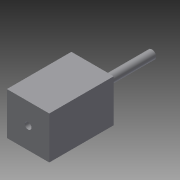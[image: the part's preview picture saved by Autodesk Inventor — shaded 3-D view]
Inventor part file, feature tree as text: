
AUTODESK INVENTOR PART (.ipt)
format: ipt  version: 2013 (Build 170138000, 138)  size: 86,528 bytes
history: native  units: in
note: dims shown in document units (in); Inventor stores cm internally (conversion verified against a paired STEP export)
features: extrude x3, sketch x3
ambient origin geometry x8: Origin, YZ Plane, XZ Plane, XY Plane, X Axis, Y Axis, Z Axis, Center Point
bodies: Solid1 (feature_tree)
feature tree (6):
  extrude  "Extrusion1"  Depth=2.5in
  extrude  "Extrusion2"  Depth=0.5in
  extrude  "Extrusion3"  Depth=1.25in
  sketch  "Sketch1"  dims[d0=2.5in d1=2.5in]
  sketch  "Sketch2"  dims[d2=3.805in d3=0.0in d4=0.5in]
  sketch  "Sketch3"  dims[d5=1.25in d6=1.25in d7=3.5in d8=0.0in d9=2.5in d10=0.3937in d11=3.5in d12=0.0in]
